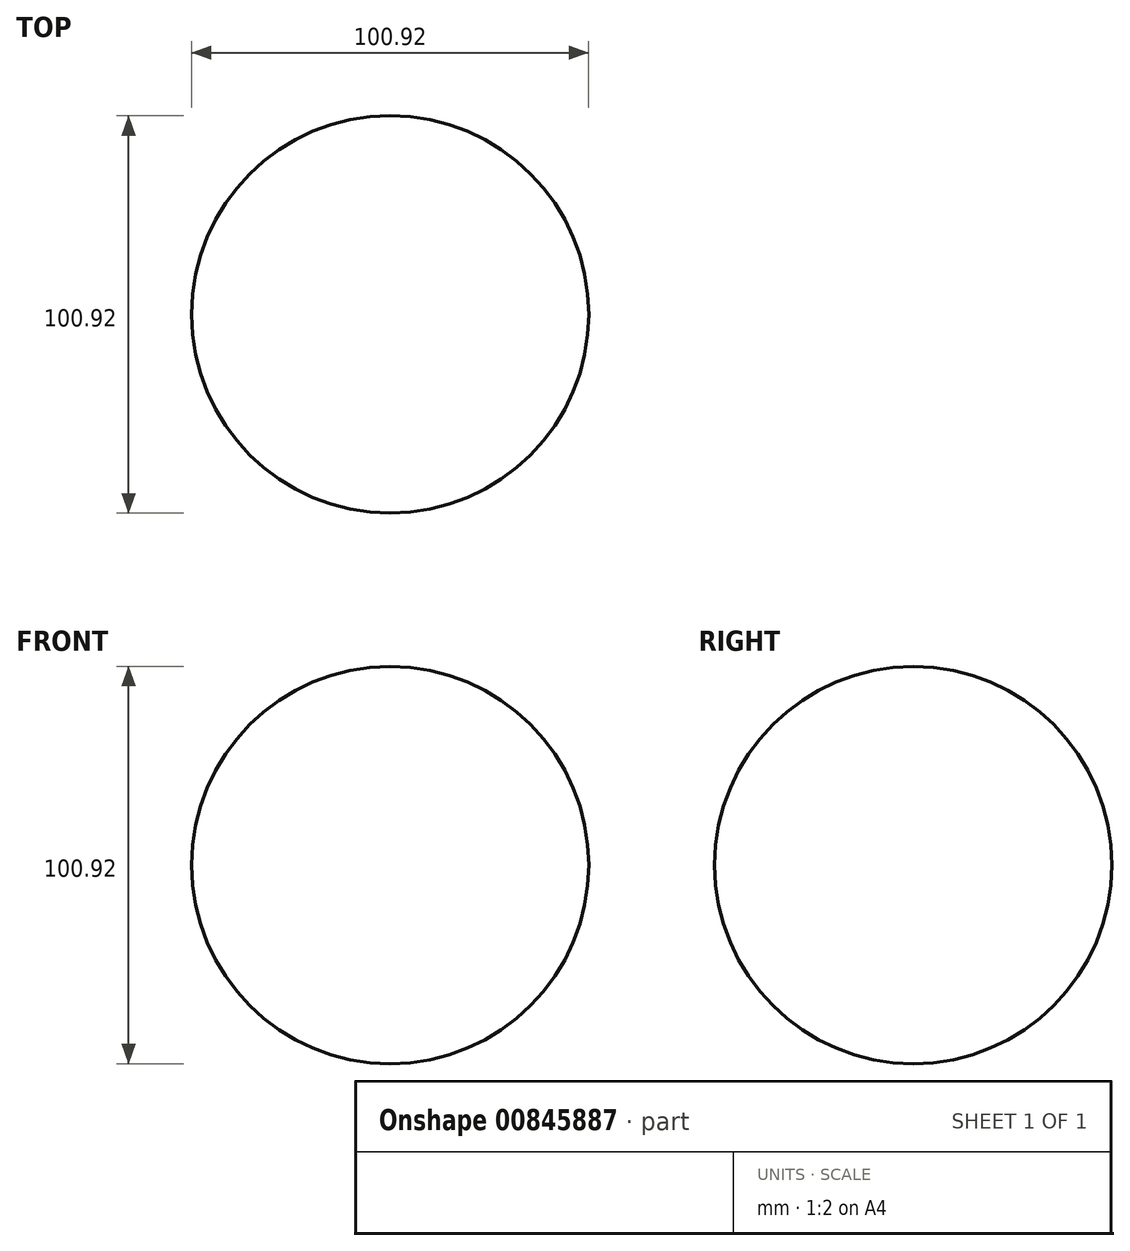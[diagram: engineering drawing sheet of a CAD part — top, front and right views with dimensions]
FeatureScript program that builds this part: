
annotation { "Feature Type Name" : "Feature", "Feature Type Description" : "" }
export const myFeature = defineFeature(function(context is Context, id is Id, definition is map)
    precondition{}
    {
        {
            var Q0;
            Q0=qCreatedBy(makeId("Front.planeOp"),FACE);
            var sketch = newSketch(context, id + "F0", { "sketchPlane" : qUnion([Q0])});
            skCircle(sketch, "E0", {"center": v(0, 0) * mm, "radius": 50.46 * mm});
            skLineSegment(sketch, "E1", {"start": v(0, 75.85) * mm, "end": v(0, -75.85) * mm});
            skSolve(sketch);
        }
        {
            var Q0;
            {var subQ0=sQuery(id+"F0.wireOp",EDGE,"E1");var subQ1=sQuery(id+"F0.wireOp",EDGE,"E0");var subQ2=makeQuery(id+"F0.imprint","INTERSECT",VERTEX,{"disambiguationData":[OD(0.0)],"derivedFrom":[subQ1,subQ0]});Q0=makeQuery(id+"F0.imprint","IMPRINT",FACE,{"disambiguationData":[TD([[makeQuery(id+"F0.imprint","IMPRINT",EDGE,{"disambiguationData":[TD([[subQ2,1.0]])],"derivedFrom":subQ1}),1.0]])]});}
            var Q1;
            Q1=sQuery(id+"F0.wireOp",EDGE,"E1");
            revolve(context, id + "F1", {"surfaceOperationType" : NewSurfaceOperationType.NEW, "entities" : qUnion([Q0]), "axis" : qUnion([Q1]), "revolveType" : RevolveType.FULL});
        }
    });
